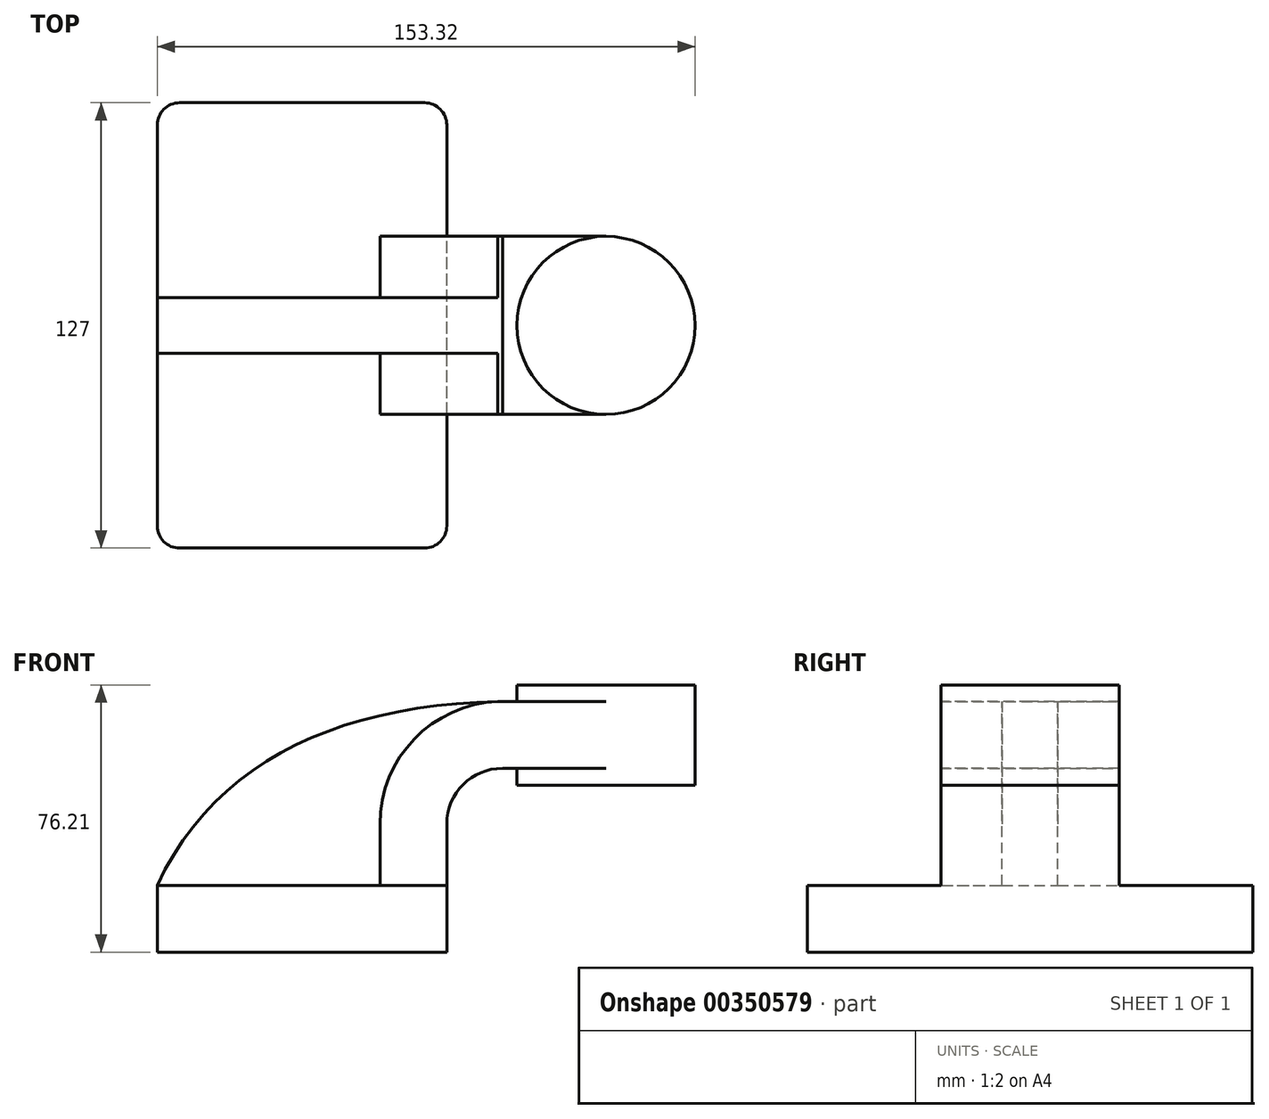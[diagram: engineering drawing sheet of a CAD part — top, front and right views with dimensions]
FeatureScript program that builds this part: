
annotation { "Feature Type Name" : "Feature", "Feature Type Description" : "" }
export const myFeature = defineFeature(function(context is Context, id is Id, definition is map)
    precondition{}
    {
        {
            var Q0;
            Q0=qCreatedBy(makeId("Front.planeOp"),FACE);
            var sketch = newSketch(context, id + "F0", { "sketchPlane" : qUnion([Q0])});
            skLineSegment(sketch, "E0.bottom", {"start": v(-41.28, 9.52) * mm, "end": v(41.28, 9.53) * mm});
            skLineSegment(sketch, "E0.top", {"start": v(-41.28, -9.53) * mm, "end": v(41.28, -9.53) * mm});
            skLineSegment(sketch, "E0.left", {"start": v(-41.28, 9.52) * mm, "end": v(-41.28, -9.53) * mm});
            skLineSegment(sketch, "E0.right", {"start": v(41.27, 9.53) * mm, "end": v(41.28, -9.52) * mm});
            skPoint(sketch, "E0.middle", {"position": v(0, 0) * mm});
            skLineSegment(sketch, "E1.bottom", {"start": v(61.24, 38.1) * mm, "end": v(112.04, 38.1) * mm});
            skLineSegment(sketch, "E1.top", {"start": v(61.24, 66.68) * mm, "end": v(112.04, 66.68) * mm});
            skLineSegment(sketch, "E1.left", {"start": v(61.24, 38.1) * mm, "end": v(61.24, 66.68) * mm});
            skLineSegment(sketch, "E1.right", {"start": v(112.04, 38.1) * mm, "end": v(112.04, 66.68) * mm});
            skPoint(sketch, "E1.middle", {"position": v(86.64, 52.39) * mm});
            skLineSegment(sketch, "E2", {"start": v(41.27, 9.53) * mm, "end": v(41.27, 27) * mm});
            skArc(sketch, "E3", {"start": v(41.27, 27) * mm, "mid": v(45.92, 38.23) * mm, "end": v(57.15, 42.88) * mm});
            skLineSegment(sketch, "E4", {"start": v(57.15, 42.88) * mm, "end": v(86.7, 42.88) * mm});
            skLineSegment(sketch, "E5.0", {"start": v(57.15, 61.93) * mm, "end": v(86.9, 61.93) * mm});
            skArc(sketch, "E5.1", {"start": v(22.22, 27) * mm, "mid": v(32.45, 51.7) * mm, "end": v(57.15, 61.93) * mm});
            skLineSegment(sketch, "E5.2", {"start": v(22.22, 9.53) * mm, "end": v(22.22, 27) * mm});
            skFitSpline(sketch, "E6", {"points": [v(-41.28, 9.52) * mm, v(57.15, 61.93) * mm], "startDerivative": vector(49.7, 105.92) * mm, "endDerivative": vector(140.67, 2.17) * mm});
            skLineSegment(sketch, "E7", {"start": v(86.64, 38.1) * mm, "end": v(86.64, 66.68) * mm});
            skSolve(sketch);
        }
        {
            var Q0;
            Q0=makeQuery(id+"F0.imprint","IMPRINT",FACE,{"disambiguationData":[TD([[makeQuery(id+"F0.imprint","IMPRINT",EDGE,{"derivedFrom":sQuery(id+"F0.wireOp",EDGE,"E0.top")}),1.0]])]});
            extrude(context, id + "F1", {"entities" : qUnion([Q0]), "depth" : 127 * mm, "symmetric" : true});
        }
        {
            var Q0;
            {var subQ1=sQuery(id+"F0.wireOp",EDGE,"E2");Q0=makeQuery(id+"F0.imprint","IMPRINT",FACE,{"disambiguationData":[TD([[makeQuery(id+"F0.imprint","IMPRINT",EDGE,{"derivedFrom":subQ1}),1.0]])]});}
            var Q1;
            {var subQ0=sQuery(id+"F0.wireOp",EDGE,"E4");var subQ1=sQuery(id+"F0.wireOp",EDGE,"E1.left");var subQ2=makeQuery(id+"F0.imprint","INTERSECT",VERTEX,{"derivedFrom":[subQ1,subQ0]});Q1=makeQuery(id+"F0.imprint","IMPRINT",FACE,{"disambiguationData":[TD([[makeQuery(id+"F0.imprint","IMPRINT",EDGE,{"disambiguationData":[TD([[subQ2,-1.0]])],"derivedFrom":subQ1}),-1.0]])]});}
            extrude(context, id + "F2", {"entities" : qUnion([Q0, Q1]), "operationType" : NewBodyOperationType.ADD, "depth" : 50.8 * mm, "symmetric" : true});
        }
        {
            var Q0;
            {var subQ3=sQuery(id+"F0.wireOp",EDGE,"E5.2");Q0=makeQuery(id+"F0.imprint","IMPRINT",FACE,{"disambiguationData":[TD([[makeQuery(id+"F0.imprint","IMPRINT",EDGE,{"derivedFrom":subQ3}),1.0]])]});}
            extrude(context, id + "F3", {"entities" : qUnion([Q0]), "operationType" : NewBodyOperationType.ADD, "depth" : 15.88 * mm, "symmetric" : true});
        }
        {
            var Q0;
            {var subQ4=sQuery(id+"F0.wireOp",EDGE,"E1.right");Q0=makeQuery(id+"F0.imprint","IMPRINT",FACE,{"disambiguationData":[TD([[makeQuery(id+"F0.imprint","IMPRINT",EDGE,{"derivedFrom":subQ4}),1.0]])]});}
            var Q1;
            Q1=sQuery(id+"F0.wireOp",EDGE,"E7");
            revolve(context, id + "F4", {"operationType" : NewBodyOperationType.ADD, "entities" : qUnion([Q0]), "axis" : qUnion([Q1]), "revolveType" : RevolveType.FULL});
        }
        {
            var Q0;
            Q0=makeQuery(id+"F1.opExtrude","CAP_EDGE",EDGE,{"disambiguationData":[OSD([sQuery(id+"F0.wireOp",EDGE,"E0.right")])],"isStart":false});
            var Q1;
            Q1=makeQuery(id+"F1.opExtrude","CAP_EDGE",EDGE,{"disambiguationData":[OSD([sQuery(id+"F0.wireOp",EDGE,"E0.left")])],"isStart":false});
            var Q2;
            Q2=makeQuery(id+"F1.opExtrude","CAP_EDGE",EDGE,{"disambiguationData":[OSD([sQuery(id+"F0.wireOp",EDGE,"E0.right")])],"isStart":true});
            var Q3;
            Q3=makeQuery(id+"F1.opExtrude","CAP_EDGE",EDGE,{"disambiguationData":[OSD([sQuery(id+"F0.wireOp",EDGE,"E0.left")])],"isStart":true});
            fillet(context, id + "F5", {"entities" : qUnion([Q0, Q1, Q2, Q3]), "radius" : 6.35 * mm, "tangentPropagation" : true, "allowEdgeOverflow" : false});
        }
    });
